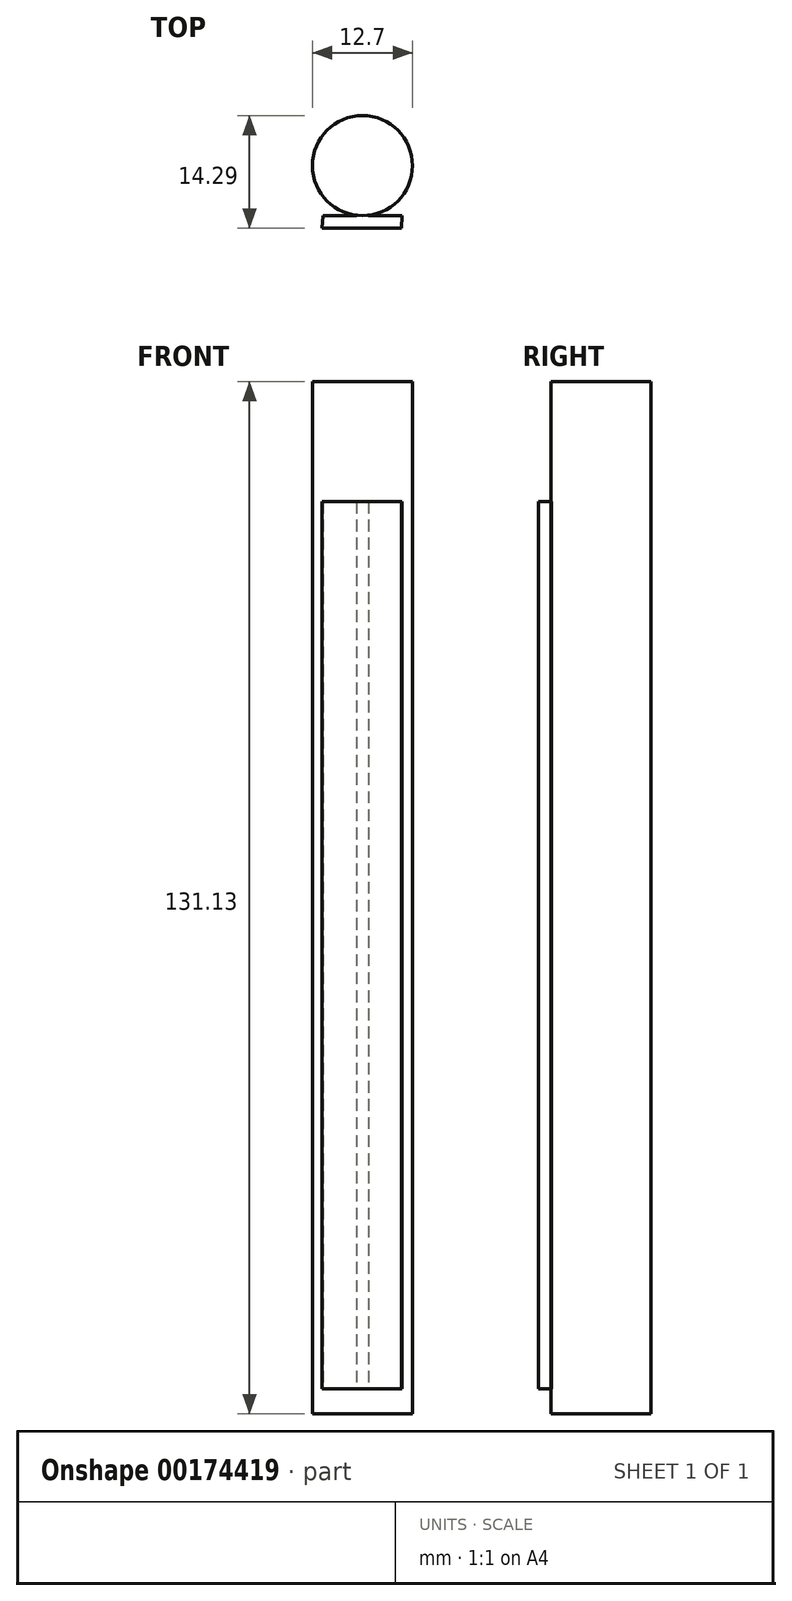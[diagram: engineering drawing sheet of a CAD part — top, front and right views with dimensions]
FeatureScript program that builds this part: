
annotation { "Feature Type Name" : "Feature", "Feature Type Description" : "" }
export const myFeature = defineFeature(function(context is Context, id is Id, definition is map)
    precondition{}
    {
        {
            var Q0;
            Q0=qCreatedBy(makeId("Top.planeOp"),FACE);
            var sketch = newSketch(context, id + "F0", { "sketchPlane" : qUnion([Q0])});
            skArc(sketch, "E0", {"start": v(0.76, -6.3) * mm, "mid": v(0, 6.35) * mm, "end": v(-0.76, -6.3) * mm});
            skLineSegment(sketch, "E1.bottom", {"start": v(4.97, -7.94) * mm, "end": v(-5.11, -7.94) * mm});
            skLineSegment(sketch, "E1.left", {"start": v(4.97, -7.94) * mm, "end": v(5.04, -6.35) * mm});
            skLineSegment(sketch, "E1.right", {"start": v(-5.11, -7.94) * mm, "end": v(-5.04, -6.35) * mm});
            skPoint(sketch, "E1.middle", {"position": v(0, -6.35) * mm});
            skLineSegment(sketch, "E2", {"start": v(-5.04, -6.35) * mm, "end": v(-0.76, -6.35) * mm});
            skPoint(sketch, "E2.endSnap0", {"position": v(5.04, -6.35) * mm});
            skPoint(sketch, "E3.orphan", {"position": v(-4.97, -4.76) * mm});
            skPoint(sketch, "E4.orphan", {"position": v(5.11, -4.76) * mm});
            skPoint(sketch, "E5.orphan", {"position": v(9.86, -6.35) * mm});
            skLineSegment(sketch, "E6", {"start": v(-0.76, -6.3) * mm, "end": v(-0.76, -6.35) * mm});
            skLineSegment(sketch, "E7", {"start": v(0.76, -6.3) * mm, "end": v(0.76, -6.35) * mm});
            skLineSegment(sketch, "E8.trimOffspring", {"start": v(0.76, -6.35) * mm, "end": v(5.04, -6.35) * mm});
            skSolve(sketch);
        }
        {
            var Q0;
            Q0 = qSketchRegion(id + "F0", true);
            extrude(context, id + "F1", {"entities" : qUnion([Q0]), "depth" : 112.7 * mm, "offsetDistance" : 25.4 * mm});
        }
        {
            var Q0;
            Q0=makeQuery(id+"F1.opExtrude","CAP_FACE",FACE,{"disambiguationData":[OSD([sQuery(id+"F0.wireOp",EDGE,"E0")])],"isStart":false});
            var sketch = newSketch(context, id + "F2", { "sketchPlane" : qUnion([Q0])});
            skCircle(sketch, "E9", {"center": v(0, 0) * mm, "radius": 6.35 * mm});
            skSolve(sketch);
        }
        {
            var Q0;
            Q0 = qSketchRegion(id + "F2", true);
            extrude(context, id + "F3", {"entities" : qUnion([Q0]), "operationType" : NewBodyOperationType.ADD, "depth" : 15.24 * mm, "offsetDistance" : 25.4 * mm});
        }
        {
            var Q0;
            Q0=makeQuery(id+"F1.opExtrude","CAP_FACE",FACE,{"disambiguationData":[OSD([sQuery(id+"F0.wireOp",EDGE,"E0")])],"isStart":true});
            var sketch = newSketch(context, id + "F4", { "sketchPlane" : qUnion([Q0])});
            skCircle(sketch, "E10", {"center": v(0, 0) * mm, "radius": 6.35 * mm});
            skSolve(sketch);
        }
        {
            var Q0;
            Q0 = qSketchRegion(id + "F4", true);
            extrude(context, id + "F5", {"entities" : qUnion([Q0]), "operationType" : NewBodyOperationType.ADD, "depth" : 3.17 * mm});
        }
    });
